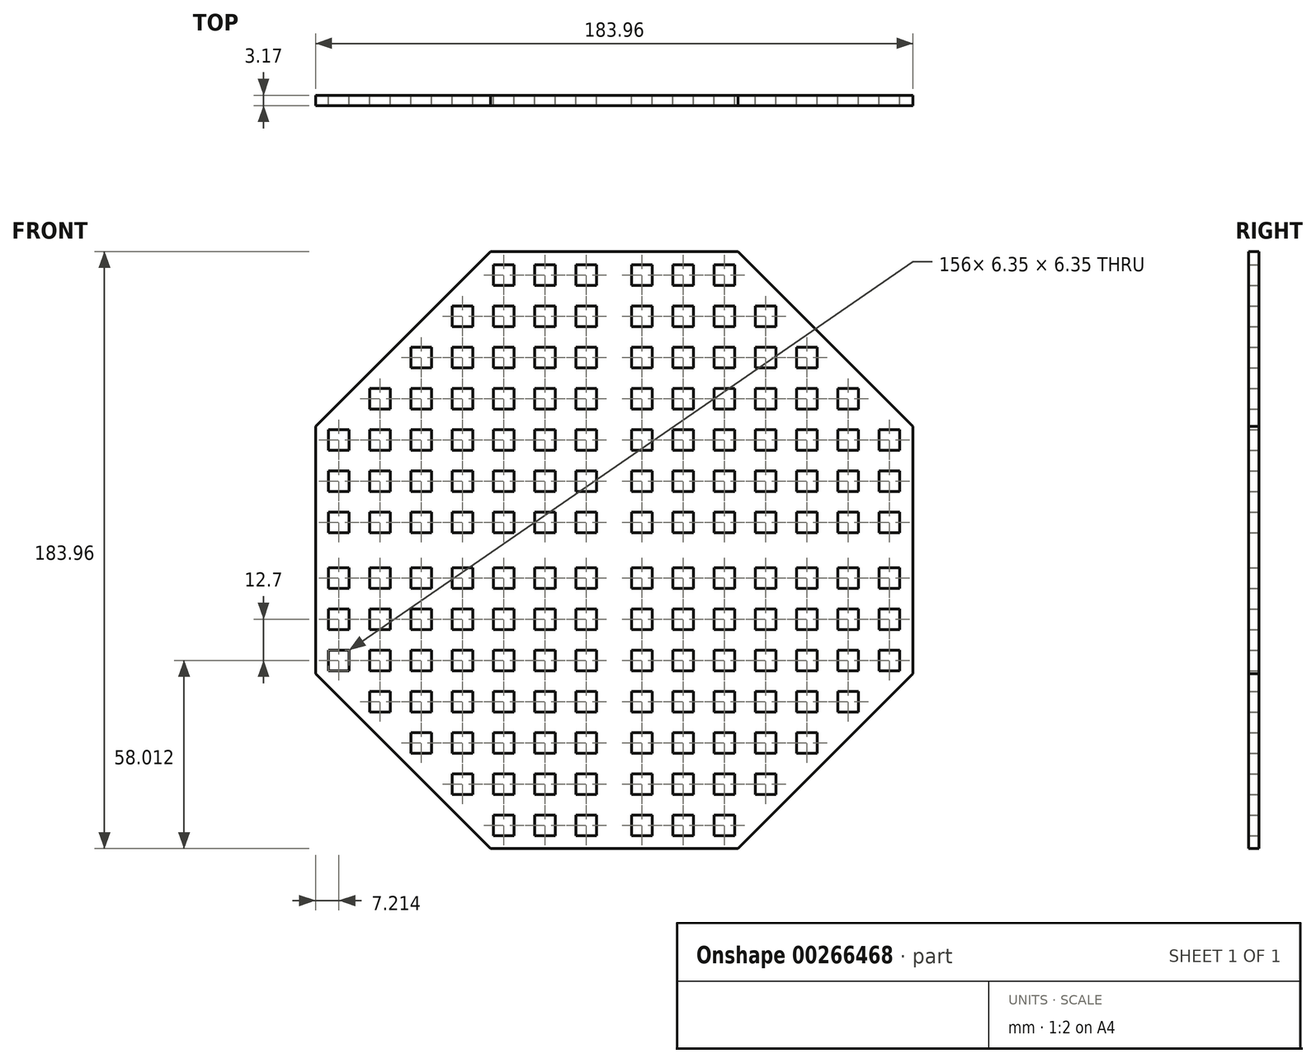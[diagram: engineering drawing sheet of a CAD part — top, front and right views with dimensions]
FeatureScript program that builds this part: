
annotation { "Feature Type Name" : "Feature", "Feature Type Description" : "" }
export const myFeature = defineFeature(function(context is Context, id is Id, definition is map)
    precondition{}
    {
        {
            var Q0;
            Q0=qCreatedBy(makeId("Front.planeOp"),FACE);
            var sketch = newSketch(context, id + "F0", { "sketchPlane" : qUnion([Q0])});
            skCircle(sketch, "E0.cCircle", {"center": v(3.14, 0) * mm, "radius": 91.98 * mm, "construction": true});
            skLineSegment(sketch, "E0.0", {"start": v(95.12, 38.1) * mm, "end": v(95.12, -38.1) * mm});
            skLineSegment(sketch, "E0.1", {"start": v(95.12, -38.1) * mm, "end": v(41.24, -91.98) * mm});
            skLineSegment(sketch, "E0.2", {"start": v(41.24, -91.98) * mm, "end": v(-34.96, -91.98) * mm});
            skLineSegment(sketch, "E0.3", {"start": v(-34.96, -91.98) * mm, "end": v(-88.84, -38.1) * mm});
            skLineSegment(sketch, "E0.4", {"start": v(-88.84, -38.1) * mm, "end": v(-88.84, 38.1) * mm});
            skLineSegment(sketch, "E0.5", {"start": v(-88.84, 38.1) * mm, "end": v(-34.96, 91.98) * mm});
            skLineSegment(sketch, "E0.6", {"start": v(-34.96, 91.98) * mm, "end": v(41.24, 91.98) * mm});
            skLineSegment(sketch, "E0.7", {"start": v(41.24, 91.98) * mm, "end": v(95.12, 38.1) * mm});
            skPoint(sketch, "E0.0.midPoint", {"position": v(95.12, 0) * mm});
            skLineSegment(sketch, "E1.0.4.0", {"start": v(-84.8, 37.14) * mm, "end": v(-78.45, 37.14) * mm});
            skLineSegment(sketch, "E1.0.4.1", {"start": v(-84.8, 37.14) * mm, "end": v(-84.8, 30.8) * mm});
            skLineSegment(sketch, "E1.0.4.2", {"start": v(-84.8, 30.8) * mm, "end": v(-78.45, 30.8) * mm});
            skLineSegment(sketch, "E1.0.4.3", {"start": v(-78.45, 37.14) * mm, "end": v(-78.45, 30.8) * mm});
            skLineSegment(sketch, "E1.0.5.0", {"start": v(-84.8, 24.44) * mm, "end": v(-78.45, 24.44) * mm});
            skLineSegment(sketch, "E1.0.5.1", {"start": v(-84.8, 24.44) * mm, "end": v(-84.8, 18.1) * mm});
            skLineSegment(sketch, "E1.0.5.2", {"start": v(-84.8, 18.1) * mm, "end": v(-78.45, 18.1) * mm});
            skLineSegment(sketch, "E1.0.5.3", {"start": v(-78.45, 24.44) * mm, "end": v(-78.45, 18.1) * mm});
            skLineSegment(sketch, "E1.0.6.0", {"start": v(-84.8, 11.74) * mm, "end": v(-78.45, 11.74) * mm});
            skLineSegment(sketch, "E1.0.6.1", {"start": v(-84.8, 11.74) * mm, "end": v(-84.8, 5.4) * mm});
            skLineSegment(sketch, "E1.0.6.2", {"start": v(-84.8, 5.4) * mm, "end": v(-78.45, 5.4) * mm});
            skLineSegment(sketch, "E1.0.6.3", {"start": v(-78.45, 11.74) * mm, "end": v(-78.45, 5.4) * mm});
            skLineSegment(sketch, "E1.1.3.0", {"start": v(-72.1, 49.84) * mm, "end": v(-65.75, 49.84) * mm});
            skLineSegment(sketch, "E1.1.3.1", {"start": v(-72.1, 49.84) * mm, "end": v(-72.1, 43.5) * mm});
            skLineSegment(sketch, "E1.1.3.2", {"start": v(-72.1, 43.5) * mm, "end": v(-65.75, 43.5) * mm});
            skLineSegment(sketch, "E1.1.3.3", {"start": v(-65.75, 49.84) * mm, "end": v(-65.75, 43.5) * mm});
            skLineSegment(sketch, "E1.1.4.0", {"start": v(-72.1, 37.14) * mm, "end": v(-65.75, 37.14) * mm});
            skLineSegment(sketch, "E1.1.4.1", {"start": v(-72.1, 37.14) * mm, "end": v(-72.1, 30.8) * mm});
            skLineSegment(sketch, "E1.1.4.2", {"start": v(-72.1, 30.8) * mm, "end": v(-65.75, 30.8) * mm});
            skLineSegment(sketch, "E1.1.4.3", {"start": v(-65.75, 37.14) * mm, "end": v(-65.75, 30.8) * mm});
            skLineSegment(sketch, "E1.1.5.0", {"start": v(-72.1, 24.44) * mm, "end": v(-65.75, 24.44) * mm});
            skLineSegment(sketch, "E1.1.5.1", {"start": v(-72.1, 24.44) * mm, "end": v(-72.1, 18.1) * mm});
            skLineSegment(sketch, "E1.1.5.2", {"start": v(-72.1, 18.1) * mm, "end": v(-65.75, 18.1) * mm});
            skLineSegment(sketch, "E1.1.5.3", {"start": v(-65.75, 24.44) * mm, "end": v(-65.75, 18.1) * mm});
            skLineSegment(sketch, "E1.1.6.0", {"start": v(-72.1, 11.74) * mm, "end": v(-65.75, 11.74) * mm});
            skLineSegment(sketch, "E1.1.6.1", {"start": v(-72.1, 11.74) * mm, "end": v(-72.1, 5.4) * mm});
            skLineSegment(sketch, "E1.1.6.2", {"start": v(-72.1, 5.4) * mm, "end": v(-65.75, 5.4) * mm});
            skLineSegment(sketch, "E1.1.6.3", {"start": v(-65.75, 11.74) * mm, "end": v(-65.75, 5.4) * mm});
            skLineSegment(sketch, "E1.2.2.0", {"start": v(-59.4, 62.54) * mm, "end": v(-53.05, 62.54) * mm});
            skLineSegment(sketch, "E1.2.2.1", {"start": v(-59.4, 62.54) * mm, "end": v(-59.4, 56.2) * mm});
            skLineSegment(sketch, "E1.2.2.2", {"start": v(-59.4, 56.2) * mm, "end": v(-53.05, 56.2) * mm});
            skLineSegment(sketch, "E1.2.2.3", {"start": v(-53.05, 62.54) * mm, "end": v(-53.05, 56.2) * mm});
            skLineSegment(sketch, "E1.2.3.0", {"start": v(-59.4, 49.84) * mm, "end": v(-53.05, 49.84) * mm});
            skLineSegment(sketch, "E1.2.3.1", {"start": v(-59.4, 49.84) * mm, "end": v(-59.4, 43.5) * mm});
            skLineSegment(sketch, "E1.2.3.2", {"start": v(-59.4, 43.5) * mm, "end": v(-53.05, 43.5) * mm});
            skLineSegment(sketch, "E1.2.3.3", {"start": v(-53.05, 49.84) * mm, "end": v(-53.05, 43.5) * mm});
            skLineSegment(sketch, "E1.2.4.0", {"start": v(-59.4, 37.14) * mm, "end": v(-53.05, 37.14) * mm});
            skLineSegment(sketch, "E1.2.4.1", {"start": v(-59.4, 37.14) * mm, "end": v(-59.4, 30.8) * mm});
            skLineSegment(sketch, "E1.2.4.2", {"start": v(-59.4, 30.8) * mm, "end": v(-53.05, 30.8) * mm});
            skLineSegment(sketch, "E1.2.4.3", {"start": v(-53.05, 37.14) * mm, "end": v(-53.05, 30.8) * mm});
            skLineSegment(sketch, "E1.2.5.0", {"start": v(-59.4, 24.44) * mm, "end": v(-53.05, 24.44) * mm});
            skLineSegment(sketch, "E1.2.5.1", {"start": v(-59.4, 24.44) * mm, "end": v(-59.4, 18.1) * mm});
            skLineSegment(sketch, "E1.2.5.2", {"start": v(-59.4, 18.1) * mm, "end": v(-53.05, 18.1) * mm});
            skLineSegment(sketch, "E1.2.5.3", {"start": v(-53.05, 24.44) * mm, "end": v(-53.05, 18.1) * mm});
            skLineSegment(sketch, "E1.2.6.0", {"start": v(-59.4, 11.74) * mm, "end": v(-53.05, 11.74) * mm});
            skLineSegment(sketch, "E1.2.6.1", {"start": v(-59.4, 11.74) * mm, "end": v(-59.4, 5.4) * mm});
            skLineSegment(sketch, "E1.2.6.2", {"start": v(-59.4, 5.4) * mm, "end": v(-53.05, 5.4) * mm});
            skLineSegment(sketch, "E1.2.6.3", {"start": v(-53.05, 11.74) * mm, "end": v(-53.05, 5.4) * mm});
            skLineSegment(sketch, "E1.3.1.0", {"start": v(-46.7, 75.24) * mm, "end": v(-40.35, 75.24) * mm});
            skLineSegment(sketch, "E1.3.1.1", {"start": v(-46.7, 75.24) * mm, "end": v(-46.7, 68.9) * mm});
            skLineSegment(sketch, "E1.3.1.2", {"start": v(-46.7, 68.9) * mm, "end": v(-40.35, 68.9) * mm});
            skLineSegment(sketch, "E1.3.1.3", {"start": v(-40.35, 75.24) * mm, "end": v(-40.35, 68.9) * mm});
            skLineSegment(sketch, "E1.3.2.0", {"start": v(-46.7, 62.54) * mm, "end": v(-40.35, 62.54) * mm});
            skLineSegment(sketch, "E1.3.2.1", {"start": v(-46.7, 62.54) * mm, "end": v(-46.7, 56.2) * mm});
            skLineSegment(sketch, "E1.3.2.2", {"start": v(-46.7, 56.2) * mm, "end": v(-40.35, 56.2) * mm});
            skLineSegment(sketch, "E1.3.2.3", {"start": v(-40.35, 62.54) * mm, "end": v(-40.35, 56.2) * mm});
            skLineSegment(sketch, "E1.3.3.0", {"start": v(-46.7, 49.84) * mm, "end": v(-40.35, 49.84) * mm});
            skLineSegment(sketch, "E1.3.3.1", {"start": v(-46.7, 49.84) * mm, "end": v(-46.7, 43.5) * mm});
            skLineSegment(sketch, "E1.3.3.2", {"start": v(-46.7, 43.5) * mm, "end": v(-40.35, 43.5) * mm});
            skLineSegment(sketch, "E1.3.3.3", {"start": v(-40.35, 49.84) * mm, "end": v(-40.35, 43.5) * mm});
            skLineSegment(sketch, "E1.3.4.0", {"start": v(-46.7, 37.14) * mm, "end": v(-40.35, 37.14) * mm});
            skLineSegment(sketch, "E1.3.4.1", {"start": v(-46.7, 37.14) * mm, "end": v(-46.7, 30.8) * mm});
            skLineSegment(sketch, "E1.3.4.2", {"start": v(-46.7, 30.8) * mm, "end": v(-40.35, 30.8) * mm});
            skLineSegment(sketch, "E1.3.4.3", {"start": v(-40.35, 37.14) * mm, "end": v(-40.35, 30.8) * mm});
            skLineSegment(sketch, "E1.3.5.0", {"start": v(-46.7, 24.44) * mm, "end": v(-40.35, 24.44) * mm});
            skLineSegment(sketch, "E1.3.5.1", {"start": v(-46.7, 24.44) * mm, "end": v(-46.7, 18.1) * mm});
            skLineSegment(sketch, "E1.3.5.2", {"start": v(-46.7, 18.1) * mm, "end": v(-40.35, 18.1) * mm});
            skLineSegment(sketch, "E1.3.5.3", {"start": v(-40.35, 24.44) * mm, "end": v(-40.35, 18.1) * mm});
            skLineSegment(sketch, "E1.3.6.0", {"start": v(-46.7, 11.74) * mm, "end": v(-40.35, 11.74) * mm});
            skLineSegment(sketch, "E1.3.6.1", {"start": v(-46.7, 11.74) * mm, "end": v(-46.7, 5.4) * mm});
            skLineSegment(sketch, "E1.3.6.2", {"start": v(-46.7, 5.4) * mm, "end": v(-40.35, 5.4) * mm});
            skLineSegment(sketch, "E1.3.6.3", {"start": v(-40.35, 11.74) * mm, "end": v(-40.35, 5.4) * mm});
            skLineSegment(sketch, "E1.4.0.0", {"start": v(-34, 87.94) * mm, "end": v(-27.65, 87.94) * mm});
            skLineSegment(sketch, "E1.4.0.1", {"start": v(-34, 87.94) * mm, "end": v(-34, 81.6) * mm});
            skLineSegment(sketch, "E1.4.0.2", {"start": v(-34, 81.6) * mm, "end": v(-27.65, 81.6) * mm});
            skLineSegment(sketch, "E1.4.0.3", {"start": v(-27.65, 87.94) * mm, "end": v(-27.65, 81.6) * mm});
            skLineSegment(sketch, "E1.4.1.0", {"start": v(-34, 75.24) * mm, "end": v(-27.65, 75.24) * mm});
            skLineSegment(sketch, "E1.4.1.1", {"start": v(-34, 75.24) * mm, "end": v(-34, 68.9) * mm});
            skLineSegment(sketch, "E1.4.1.2", {"start": v(-34, 68.9) * mm, "end": v(-27.65, 68.9) * mm});
            skLineSegment(sketch, "E1.4.1.3", {"start": v(-27.65, 75.24) * mm, "end": v(-27.65, 68.9) * mm});
            skLineSegment(sketch, "E1.4.2.0", {"start": v(-34, 62.54) * mm, "end": v(-27.65, 62.54) * mm});
            skLineSegment(sketch, "E1.4.2.1", {"start": v(-34, 62.54) * mm, "end": v(-34, 56.2) * mm});
            skLineSegment(sketch, "E1.4.2.2", {"start": v(-34, 56.2) * mm, "end": v(-27.65, 56.2) * mm});
            skLineSegment(sketch, "E1.4.2.3", {"start": v(-27.65, 62.54) * mm, "end": v(-27.65, 56.2) * mm});
            skLineSegment(sketch, "E1.4.3.0", {"start": v(-34, 49.84) * mm, "end": v(-27.65, 49.84) * mm});
            skLineSegment(sketch, "E1.4.3.1", {"start": v(-34, 49.84) * mm, "end": v(-34, 43.5) * mm});
            skLineSegment(sketch, "E1.4.3.2", {"start": v(-34, 43.5) * mm, "end": v(-27.65, 43.5) * mm});
            skLineSegment(sketch, "E1.4.3.3", {"start": v(-27.65, 49.84) * mm, "end": v(-27.65, 43.5) * mm});
            skLineSegment(sketch, "E1.4.4.0", {"start": v(-34, 37.14) * mm, "end": v(-27.65, 37.14) * mm});
            skLineSegment(sketch, "E1.4.4.1", {"start": v(-34, 37.14) * mm, "end": v(-34, 30.8) * mm});
            skLineSegment(sketch, "E1.4.4.2", {"start": v(-34, 30.8) * mm, "end": v(-27.65, 30.8) * mm});
            skLineSegment(sketch, "E1.4.4.3", {"start": v(-27.65, 37.14) * mm, "end": v(-27.65, 30.8) * mm});
            skLineSegment(sketch, "E1.4.5.0", {"start": v(-34, 24.44) * mm, "end": v(-27.65, 24.44) * mm});
            skLineSegment(sketch, "E1.4.5.1", {"start": v(-34, 24.44) * mm, "end": v(-34, 18.1) * mm});
            skLineSegment(sketch, "E1.4.5.2", {"start": v(-34, 18.1) * mm, "end": v(-27.65, 18.1) * mm});
            skLineSegment(sketch, "E1.4.5.3", {"start": v(-27.65, 24.44) * mm, "end": v(-27.65, 18.1) * mm});
            skLineSegment(sketch, "E1.4.6.0", {"start": v(-34, 11.74) * mm, "end": v(-27.65, 11.74) * mm});
            skLineSegment(sketch, "E1.4.6.1", {"start": v(-34, 11.74) * mm, "end": v(-34, 5.4) * mm});
            skLineSegment(sketch, "E1.4.6.2", {"start": v(-34, 5.4) * mm, "end": v(-27.65, 5.4) * mm});
            skLineSegment(sketch, "E1.4.6.3", {"start": v(-27.65, 11.74) * mm, "end": v(-27.65, 5.4) * mm});
            skLineSegment(sketch, "E1.5.0.0", {"start": v(-21.3, 87.94) * mm, "end": v(-14.95, 87.94) * mm});
            skLineSegment(sketch, "E1.5.0.1", {"start": v(-21.3, 87.94) * mm, "end": v(-21.3, 81.6) * mm});
            skLineSegment(sketch, "E1.5.0.2", {"start": v(-21.3, 81.6) * mm, "end": v(-14.95, 81.6) * mm});
            skLineSegment(sketch, "E1.5.0.3", {"start": v(-14.95, 87.94) * mm, "end": v(-14.95, 81.6) * mm});
            skLineSegment(sketch, "E1.5.1.0", {"start": v(-21.3, 75.24) * mm, "end": v(-14.95, 75.24) * mm});
            skLineSegment(sketch, "E1.5.1.1", {"start": v(-21.3, 75.24) * mm, "end": v(-21.3, 68.9) * mm});
            skLineSegment(sketch, "E1.5.1.2", {"start": v(-21.3, 68.9) * mm, "end": v(-14.95, 68.9) * mm});
            skLineSegment(sketch, "E1.5.1.3", {"start": v(-14.95, 75.24) * mm, "end": v(-14.95, 68.9) * mm});
            skLineSegment(sketch, "E1.5.2.0", {"start": v(-21.3, 62.54) * mm, "end": v(-14.95, 62.54) * mm});
            skLineSegment(sketch, "E1.5.2.1", {"start": v(-21.3, 62.54) * mm, "end": v(-21.3, 56.2) * mm});
            skLineSegment(sketch, "E1.5.2.2", {"start": v(-21.3, 56.2) * mm, "end": v(-14.95, 56.2) * mm});
            skLineSegment(sketch, "E1.5.2.3", {"start": v(-14.95, 62.54) * mm, "end": v(-14.95, 56.2) * mm});
            skLineSegment(sketch, "E1.5.3.0", {"start": v(-21.3, 49.84) * mm, "end": v(-14.95, 49.84) * mm});
            skLineSegment(sketch, "E1.5.3.1", {"start": v(-21.3, 49.84) * mm, "end": v(-21.3, 43.5) * mm});
            skLineSegment(sketch, "E1.5.3.2", {"start": v(-21.3, 43.5) * mm, "end": v(-14.95, 43.5) * mm});
            skLineSegment(sketch, "E1.5.3.3", {"start": v(-14.95, 49.84) * mm, "end": v(-14.95, 43.5) * mm});
            skLineSegment(sketch, "E1.5.4.0", {"start": v(-21.3, 37.14) * mm, "end": v(-14.95, 37.14) * mm});
            skLineSegment(sketch, "E1.5.4.1", {"start": v(-21.3, 37.14) * mm, "end": v(-21.3, 30.8) * mm});
            skLineSegment(sketch, "E1.5.4.2", {"start": v(-21.3, 30.8) * mm, "end": v(-14.95, 30.8) * mm});
            skLineSegment(sketch, "E1.5.4.3", {"start": v(-14.95, 37.14) * mm, "end": v(-14.95, 30.8) * mm});
            skLineSegment(sketch, "E1.5.5.0", {"start": v(-21.3, 24.44) * mm, "end": v(-14.95, 24.44) * mm});
            skLineSegment(sketch, "E1.5.5.1", {"start": v(-21.3, 24.44) * mm, "end": v(-21.3, 18.1) * mm});
            skLineSegment(sketch, "E1.5.5.2", {"start": v(-21.3, 18.1) * mm, "end": v(-14.95, 18.1) * mm});
            skLineSegment(sketch, "E1.5.5.3", {"start": v(-14.95, 24.44) * mm, "end": v(-14.95, 18.1) * mm});
            skLineSegment(sketch, "E1.5.6.0", {"start": v(-21.3, 11.74) * mm, "end": v(-14.95, 11.74) * mm});
            skLineSegment(sketch, "E1.5.6.1", {"start": v(-21.3, 11.74) * mm, "end": v(-21.3, 5.4) * mm});
            skLineSegment(sketch, "E1.5.6.2", {"start": v(-21.3, 5.4) * mm, "end": v(-14.95, 5.4) * mm});
            skLineSegment(sketch, "E1.5.6.3", {"start": v(-14.95, 11.74) * mm, "end": v(-14.95, 5.4) * mm});
            skLineSegment(sketch, "E1.6.0.0", {"start": v(-8.6, 87.94) * mm, "end": v(-2.25, 87.94) * mm});
            skLineSegment(sketch, "E1.6.0.1", {"start": v(-8.6, 87.94) * mm, "end": v(-8.6, 81.6) * mm});
            skLineSegment(sketch, "E1.6.0.2", {"start": v(-8.6, 81.6) * mm, "end": v(-2.25, 81.6) * mm});
            skLineSegment(sketch, "E1.6.0.3", {"start": v(-2.25, 87.94) * mm, "end": v(-2.25, 81.6) * mm});
            skLineSegment(sketch, "E1.6.1.0", {"start": v(-8.6, 75.24) * mm, "end": v(-2.25, 75.24) * mm});
            skLineSegment(sketch, "E1.6.1.1", {"start": v(-8.6, 75.24) * mm, "end": v(-8.6, 68.9) * mm});
            skLineSegment(sketch, "E1.6.1.2", {"start": v(-8.6, 68.9) * mm, "end": v(-2.25, 68.9) * mm});
            skLineSegment(sketch, "E1.6.1.3", {"start": v(-2.25, 75.24) * mm, "end": v(-2.25, 68.9) * mm});
            skLineSegment(sketch, "E1.6.2.0", {"start": v(-8.6, 62.54) * mm, "end": v(-2.25, 62.54) * mm});
            skLineSegment(sketch, "E1.6.2.1", {"start": v(-8.6, 62.54) * mm, "end": v(-8.6, 56.2) * mm});
            skLineSegment(sketch, "E1.6.2.2", {"start": v(-8.6, 56.2) * mm, "end": v(-2.25, 56.2) * mm});
            skLineSegment(sketch, "E1.6.2.3", {"start": v(-2.25, 62.54) * mm, "end": v(-2.25, 56.2) * mm});
            skLineSegment(sketch, "E1.6.3.0", {"start": v(-8.6, 49.84) * mm, "end": v(-2.25, 49.84) * mm});
            skLineSegment(sketch, "E1.6.3.1", {"start": v(-8.6, 49.84) * mm, "end": v(-8.6, 43.5) * mm});
            skLineSegment(sketch, "E1.6.3.2", {"start": v(-8.6, 43.5) * mm, "end": v(-2.25, 43.5) * mm});
            skLineSegment(sketch, "E1.6.3.3", {"start": v(-2.25, 49.84) * mm, "end": v(-2.25, 43.5) * mm});
            skLineSegment(sketch, "E1.6.4.0", {"start": v(-8.6, 37.14) * mm, "end": v(-2.25, 37.14) * mm});
            skLineSegment(sketch, "E1.6.4.1", {"start": v(-8.6, 37.14) * mm, "end": v(-8.6, 30.8) * mm});
            skLineSegment(sketch, "E1.6.4.2", {"start": v(-8.6, 30.8) * mm, "end": v(-2.25, 30.8) * mm});
            skLineSegment(sketch, "E1.6.4.3", {"start": v(-2.25, 37.14) * mm, "end": v(-2.25, 30.8) * mm});
            skLineSegment(sketch, "E1.6.5.0", {"start": v(-8.6, 24.44) * mm, "end": v(-2.25, 24.44) * mm});
            skLineSegment(sketch, "E1.6.5.1", {"start": v(-8.6, 24.44) * mm, "end": v(-8.6, 18.1) * mm});
            skLineSegment(sketch, "E1.6.5.2", {"start": v(-8.6, 18.1) * mm, "end": v(-2.25, 18.1) * mm});
            skLineSegment(sketch, "E1.6.5.3", {"start": v(-2.25, 24.44) * mm, "end": v(-2.25, 18.1) * mm});
            skLineSegment(sketch, "E1.6.6.0", {"start": v(-8.6, 11.74) * mm, "end": v(-2.25, 11.74) * mm});
            skLineSegment(sketch, "E1.6.6.1", {"start": v(-8.6, 11.74) * mm, "end": v(-8.6, 5.4) * mm});
            skLineSegment(sketch, "E1.6.6.2", {"start": v(-8.6, 5.4) * mm, "end": v(-2.25, 5.4) * mm});
            skLineSegment(sketch, "E1.6.6.3", {"start": v(-2.25, 11.74) * mm, "end": v(-2.25, 5.4) * mm});
            skLineSegment(sketch, "E2.MirrorCS", {"start": v(52.99, 68.9) * mm, "end": v(46.64, 68.9) * mm});
            skLineSegment(sketch, "E3.MirrorCS", {"start": v(59.34, 62.54) * mm, "end": v(59.34, 56.2) * mm});
            skLineSegment(sketch, "E4.MirrorCS", {"start": v(33.94, 75.24) * mm, "end": v(33.94, 68.9) * mm});
            skLineSegment(sketch, "E5.MirrorCS", {"start": v(21.24, 62.54) * mm, "end": v(21.24, 56.2) * mm});
            skLineSegment(sketch, "E6.MirrorCS", {"start": v(33.94, 24.44) * mm, "end": v(33.94, 18.1) * mm});
            skLineSegment(sketch, "E7.MirrorCS", {"start": v(72.04, 49.84) * mm, "end": v(72.04, 43.5) * mm});
            skLineSegment(sketch, "E8.MirrorCS", {"start": v(21.24, 11.74) * mm, "end": v(21.24, 5.4) * mm});
            skLineSegment(sketch, "E9.MirrorCS", {"start": v(8.54, 49.84) * mm, "end": v(8.54, 43.5) * mm});
            skLineSegment(sketch, "E10.MirrorCS", {"start": v(84.74, 24.44) * mm, "end": v(84.74, 18.1) * mm});
            skLineSegment(sketch, "E11.MirrorCS", {"start": v(46.64, 11.74) * mm, "end": v(46.64, 5.4) * mm});
            skLineSegment(sketch, "E12.MirrorCS", {"start": v(46.64, 62.54) * mm, "end": v(46.64, 56.2) * mm});
            skLineSegment(sketch, "E13.MirrorCS", {"start": v(72.04, 24.44) * mm, "end": v(72.04, 18.1) * mm});
            skLineSegment(sketch, "E14.MirrorCS", {"start": v(52.99, 62.54) * mm, "end": v(46.64, 62.54) * mm});
            skLineSegment(sketch, "E15.MirrorCS", {"start": v(40.29, 5.4) * mm, "end": v(33.94, 5.4) * mm});
            skLineSegment(sketch, "E16.MirrorCS", {"start": v(40.29, 56.2) * mm, "end": v(33.94, 56.2) * mm});
            skLineSegment(sketch, "E17.MirrorCS", {"start": v(27.59, 24.44) * mm, "end": v(27.59, 18.1) * mm});
            skLineSegment(sketch, "E18.MirrorCS", {"start": v(52.99, 18.1) * mm, "end": v(46.64, 18.1) * mm});
            skLineSegment(sketch, "E19.MirrorCS", {"start": v(52.99, 11.74) * mm, "end": v(46.64, 11.74) * mm});
            skLineSegment(sketch, "E20.MirrorCS", {"start": v(52.99, 24.44) * mm, "end": v(46.64, 24.44) * mm});
            skLineSegment(sketch, "E21.MirrorCS", {"start": v(46.64, 75.24) * mm, "end": v(46.64, 68.9) * mm});
            skLineSegment(sketch, "E22.MirrorCS", {"start": v(14.89, 75.24) * mm, "end": v(14.89, 68.9) * mm});
            skLineSegment(sketch, "E23.MirrorCS", {"start": v(59.34, 49.84) * mm, "end": v(59.34, 43.5) * mm});
            skLineSegment(sketch, "E24.MirrorCS", {"start": v(52.99, 37.14) * mm, "end": v(46.64, 37.14) * mm});
            skLineSegment(sketch, "E25.MirrorCS", {"start": v(84.74, 11.74) * mm, "end": v(84.74, 5.4) * mm});
            skLineSegment(sketch, "E26.MirrorCS", {"start": v(46.64, 49.84) * mm, "end": v(46.64, 43.5) * mm});
            skLineSegment(sketch, "E27.MirrorCS", {"start": v(40.29, 30.8) * mm, "end": v(33.94, 30.8) * mm});
            skLineSegment(sketch, "E28.MirrorCS", {"start": v(33.94, 62.54) * mm, "end": v(33.94, 56.2) * mm});
            skLineSegment(sketch, "E29.MirrorCS", {"start": v(40.29, 49.84) * mm, "end": v(33.94, 49.84) * mm});
            skLineSegment(sketch, "E30.MirrorCS", {"start": v(27.59, 49.84) * mm, "end": v(27.59, 43.5) * mm});
            skLineSegment(sketch, "E31.MirrorCS", {"start": v(59.34, 24.44) * mm, "end": v(59.34, 18.1) * mm});
            skLineSegment(sketch, "E32.MirrorCS", {"start": v(72.04, 11.74) * mm, "end": v(72.04, 5.4) * mm});
            skLineSegment(sketch, "E33.MirrorCS", {"start": v(14.89, 62.54) * mm, "end": v(14.89, 56.2) * mm});
            skLineSegment(sketch, "E34.MirrorCS", {"start": v(52.99, 43.5) * mm, "end": v(46.64, 43.5) * mm});
            skLineSegment(sketch, "E35.MirrorCS", {"start": v(40.29, 81.6) * mm, "end": v(33.94, 81.6) * mm});
            skLineSegment(sketch, "E36.MirrorCS", {"start": v(33.94, 11.74) * mm, "end": v(33.94, 5.4) * mm});
            skLineSegment(sketch, "E37.MirrorCS", {"start": v(91.09, 5.4) * mm, "end": v(84.74, 5.4) * mm});
            skLineSegment(sketch, "E38.MirrorCS", {"start": v(21.24, 49.84) * mm, "end": v(21.24, 43.5) * mm});
            skLineSegment(sketch, "E39.MirrorCS", {"start": v(52.99, 75.24) * mm, "end": v(46.64, 75.24) * mm});
            skLineSegment(sketch, "E40.MirrorCS", {"start": v(21.24, 24.44) * mm, "end": v(21.24, 18.1) * mm});
            skLineSegment(sketch, "E41.MirrorCS", {"start": v(8.54, 62.54) * mm, "end": v(8.54, 56.2) * mm});
            skLineSegment(sketch, "E42.MirrorCS", {"start": v(21.24, 75.24) * mm, "end": v(21.24, 68.9) * mm});
            skLineSegment(sketch, "E43.MirrorCS", {"start": v(8.54, 11.74) * mm, "end": v(8.54, 5.4) * mm});
            skLineSegment(sketch, "E44.MirrorCS", {"start": v(52.99, 11.74) * mm, "end": v(52.99, 5.4) * mm});
            skLineSegment(sketch, "E45.MirrorCS", {"start": v(52.99, 24.44) * mm, "end": v(52.99, 18.1) * mm});
            skLineSegment(sketch, "E46.MirrorCS", {"start": v(52.99, 62.54) * mm, "end": v(52.99, 56.2) * mm});
            skLineSegment(sketch, "E47.MirrorCS", {"start": v(46.64, 24.44) * mm, "end": v(46.64, 18.1) * mm});
            skLineSegment(sketch, "E48.MirrorCS", {"start": v(27.59, 75.24) * mm, "end": v(27.59, 68.9) * mm});
            skLineSegment(sketch, "E49.MirrorCS", {"start": v(65.69, 24.44) * mm, "end": v(65.69, 18.1) * mm});
            skLineSegment(sketch, "E50.MirrorCS", {"start": v(14.89, 11.74) * mm, "end": v(14.89, 5.4) * mm});
            skLineSegment(sketch, "E51.MirrorCS", {"start": v(52.99, 49.84) * mm, "end": v(52.99, 43.5) * mm});
            skLineSegment(sketch, "E52.MirrorCS", {"start": v(91.09, 11.74) * mm, "end": v(91.09, 5.4) * mm});
            skLineSegment(sketch, "E53.MirrorCS", {"start": v(78.39, 11.74) * mm, "end": v(78.39, 5.4) * mm});
            skLineSegment(sketch, "E54.MirrorCS", {"start": v(40.29, 75.24) * mm, "end": v(40.29, 68.9) * mm});
            skLineSegment(sketch, "E55.MirrorCS", {"start": v(78.39, 49.84) * mm, "end": v(78.39, 43.5) * mm});
            skLineSegment(sketch, "E56.MirrorCS", {"start": v(65.69, 11.74) * mm, "end": v(65.69, 5.4) * mm});
            skLineSegment(sketch, "E57.MirrorCS", {"start": v(65.69, 62.54) * mm, "end": v(65.69, 56.2) * mm});
            skLineSegment(sketch, "E58.MirrorCS", {"start": v(14.89, 49.84) * mm, "end": v(14.89, 43.5) * mm});
            skLineSegment(sketch, "E59.MirrorCS", {"start": v(27.59, 11.74) * mm, "end": v(27.59, 5.4) * mm});
            skLineSegment(sketch, "E60.MirrorCS", {"start": v(27.59, 62.54) * mm, "end": v(27.59, 56.2) * mm});
            skLineSegment(sketch, "E61.MirrorCS", {"start": v(40.29, 24.44) * mm, "end": v(40.29, 18.1) * mm});
            skLineSegment(sketch, "E62.MirrorCS", {"start": v(40.29, 62.54) * mm, "end": v(40.29, 56.2) * mm});
            skLineSegment(sketch, "E63.MirrorCS", {"start": v(40.29, 24.44) * mm, "end": v(33.94, 24.44) * mm});
            skLineSegment(sketch, "E64.MirrorCS", {"start": v(78.39, 24.44) * mm, "end": v(78.39, 18.1) * mm});
            skLineSegment(sketch, "E65.MirrorCS", {"start": v(40.29, 49.84) * mm, "end": v(40.29, 43.5) * mm});
            skLineSegment(sketch, "E66.MirrorCS", {"start": v(40.29, 37.14) * mm, "end": v(33.94, 37.14) * mm});
            skLineSegment(sketch, "E67.MirrorCS", {"start": v(59.34, 11.74) * mm, "end": v(59.34, 5.4) * mm});
            skLineSegment(sketch, "E68.MirrorCS", {"start": v(52.99, 49.84) * mm, "end": v(46.64, 49.84) * mm});
            skLineSegment(sketch, "E69.MirrorCS", {"start": v(40.29, 18.1) * mm, "end": v(33.94, 18.1) * mm});
            skLineSegment(sketch, "E70.MirrorCS", {"start": v(40.29, 68.9) * mm, "end": v(33.94, 68.9) * mm});
            skLineSegment(sketch, "E71.MirrorCS", {"start": v(52.99, 30.8) * mm, "end": v(46.64, 30.8) * mm});
            skLineSegment(sketch, "E72.MirrorCS", {"start": v(8.54, 24.44) * mm, "end": v(8.54, 18.1) * mm});
            skLineSegment(sketch, "E73.MirrorCS", {"start": v(33.94, 49.84) * mm, "end": v(33.94, 43.5) * mm});
            skLineSegment(sketch, "E74.MirrorCS", {"start": v(40.29, 62.54) * mm, "end": v(33.94, 62.54) * mm});
            skLineSegment(sketch, "E75.MirrorCS", {"start": v(40.29, 11.74) * mm, "end": v(40.29, 5.4) * mm});
            skLineSegment(sketch, "E76.MirrorCS", {"start": v(40.29, 43.5) * mm, "end": v(33.94, 43.5) * mm});
            skLineSegment(sketch, "E77.MirrorCS", {"start": v(8.54, 75.24) * mm, "end": v(8.54, 68.9) * mm});
            skLineSegment(sketch, "E78.MirrorCS", {"start": v(91.09, 24.44) * mm, "end": v(84.74, 24.44) * mm});
            skLineSegment(sketch, "E79.MirrorCS", {"start": v(14.89, 24.44) * mm, "end": v(14.89, 18.1) * mm});
            skLineSegment(sketch, "E80.MirrorCS", {"start": v(91.09, 30.8) * mm, "end": v(84.74, 30.8) * mm});
            skLineSegment(sketch, "E81.MirrorCS", {"start": v(40.29, 11.74) * mm, "end": v(33.94, 11.74) * mm});
            skLineSegment(sketch, "E82.MirrorCS", {"start": v(40.29, 87.94) * mm, "end": v(33.94, 87.94) * mm});
            skLineSegment(sketch, "E83.MirrorCS", {"start": v(91.09, 11.74) * mm, "end": v(84.74, 11.74) * mm});
            skLineSegment(sketch, "E84.MirrorCS", {"start": v(91.09, 24.44) * mm, "end": v(91.09, 18.1) * mm});
            skLineSegment(sketch, "E85.MirrorCS", {"start": v(52.99, 5.4) * mm, "end": v(46.64, 5.4) * mm});
            skLineSegment(sketch, "E86.MirrorCS", {"start": v(52.99, 56.2) * mm, "end": v(46.64, 56.2) * mm});
            skLineSegment(sketch, "E87.MirrorCS", {"start": v(40.29, 75.24) * mm, "end": v(33.94, 75.24) * mm});
            skLineSegment(sketch, "E88.MirrorCS", {"start": v(91.09, 18.1) * mm, "end": v(84.74, 18.1) * mm});
            skLineSegment(sketch, "E89.MirrorCS", {"start": v(91.09, 37.14) * mm, "end": v(84.74, 37.14) * mm});
            skLineSegment(sketch, "E90.MirrorCS", {"start": v(65.69, 49.84) * mm, "end": v(65.69, 43.5) * mm});
            skLineSegment(sketch, "E91.MirrorCS", {"start": v(52.99, 75.24) * mm, "end": v(52.99, 68.9) * mm});
            skLineSegment(sketch, "E92.MirrorCS", {"start": v(84.74, 37.14) * mm, "end": v(84.74, 30.8) * mm});
            skLineSegment(sketch, "E93.MirrorCS", {"start": v(46.64, 37.14) * mm, "end": v(46.64, 30.8) * mm});
            skLineSegment(sketch, "E94.MirrorCS", {"start": v(59.34, 37.14) * mm, "end": v(59.34, 30.8) * mm});
            skLineSegment(sketch, "E95.MirrorCS", {"start": v(14.89, 30.8) * mm, "end": v(8.54, 30.8) * mm});
            skLineSegment(sketch, "E96.MirrorCS", {"start": v(14.89, 81.6) * mm, "end": v(8.54, 81.6) * mm});
            skLineSegment(sketch, "E97.MirrorCS", {"start": v(78.39, 30.8) * mm, "end": v(72.04, 30.8) * mm});
            skLineSegment(sketch, "E98.MirrorCS", {"start": v(27.59, 43.5) * mm, "end": v(21.24, 43.5) * mm});
            skLineSegment(sketch, "E99.MirrorCS", {"start": v(78.39, 24.44) * mm, "end": v(72.04, 24.44) * mm});
            skLineSegment(sketch, "E100.MirrorCS", {"start": v(14.89, 75.24) * mm, "end": v(8.54, 75.24) * mm});
            skLineSegment(sketch, "E101.MirrorCS", {"start": v(14.89, 87.94) * mm, "end": v(8.54, 87.94) * mm});
            skLineSegment(sketch, "E102.MirrorCS", {"start": v(14.89, 37.14) * mm, "end": v(8.54, 37.14) * mm});
            skLineSegment(sketch, "E103.MirrorCS", {"start": v(65.69, 43.5) * mm, "end": v(59.34, 43.5) * mm});
            skLineSegment(sketch, "E104.MirrorCS", {"start": v(72.04, 37.14) * mm, "end": v(72.04, 30.8) * mm});
            skLineSegment(sketch, "E105.MirrorCS", {"start": v(78.39, 49.84) * mm, "end": v(72.04, 49.84) * mm});
            skLineSegment(sketch, "E106.MirrorCS", {"start": v(33.94, 87.94) * mm, "end": v(33.94, 81.6) * mm});
            skLineSegment(sketch, "E107.MirrorCS", {"start": v(27.59, 87.94) * mm, "end": v(21.24, 87.94) * mm});
            skLineSegment(sketch, "E108.MirrorCS", {"start": v(65.69, 30.8) * mm, "end": v(59.34, 30.8) * mm});
            skLineSegment(sketch, "E109.MirrorCS", {"start": v(14.89, 5.4) * mm, "end": v(8.54, 5.4) * mm});
            skLineSegment(sketch, "E110.MirrorCS", {"start": v(27.59, 68.9) * mm, "end": v(21.24, 68.9) * mm});
            skLineSegment(sketch, "E111.MirrorCS", {"start": v(27.59, 18.1) * mm, "end": v(21.24, 18.1) * mm});
            skLineSegment(sketch, "E112.MirrorCS", {"start": v(8.54, 37.14) * mm, "end": v(8.54, 30.8) * mm});
            skLineSegment(sketch, "E113.MirrorCS", {"start": v(65.69, 37.14) * mm, "end": v(59.34, 37.14) * mm});
            skLineSegment(sketch, "E114.MirrorCS", {"start": v(65.69, 18.1) * mm, "end": v(59.34, 18.1) * mm});
            skLineSegment(sketch, "E115.MirrorCS", {"start": v(27.59, 37.14) * mm, "end": v(21.24, 37.14) * mm});
            skLineSegment(sketch, "E116.MirrorCS", {"start": v(33.94, 37.14) * mm, "end": v(33.94, 30.8) * mm});
            skLineSegment(sketch, "E117.MirrorCS", {"start": v(8.54, 87.94) * mm, "end": v(8.54, 81.6) * mm});
            skLineSegment(sketch, "E118.MirrorCS", {"start": v(40.29, 37.14) * mm, "end": v(40.29, 30.8) * mm});
            skLineSegment(sketch, "E119.MirrorCS", {"start": v(40.29, 87.94) * mm, "end": v(40.29, 81.6) * mm});
            skLineSegment(sketch, "E120.MirrorCS", {"start": v(14.89, 56.2) * mm, "end": v(8.54, 56.2) * mm});
            skLineSegment(sketch, "E121.MirrorCS", {"start": v(78.39, 5.4) * mm, "end": v(72.04, 5.4) * mm});
            skLineSegment(sketch, "E122.MirrorCS", {"start": v(65.69, 11.74) * mm, "end": v(59.34, 11.74) * mm});
            skLineSegment(sketch, "E123.MirrorCS", {"start": v(65.69, 62.54) * mm, "end": v(59.34, 62.54) * mm});
            skLineSegment(sketch, "E124.MirrorCS", {"start": v(14.89, 49.84) * mm, "end": v(8.54, 49.84) * mm});
            skLineSegment(sketch, "E125.MirrorCS", {"start": v(52.99, 37.14) * mm, "end": v(52.99, 30.8) * mm});
            skLineSegment(sketch, "E126.MirrorCS", {"start": v(27.59, 62.54) * mm, "end": v(21.24, 62.54) * mm});
            skLineSegment(sketch, "E127.MirrorCS", {"start": v(27.59, 11.74) * mm, "end": v(21.24, 11.74) * mm});
            skLineSegment(sketch, "E128.MirrorCS", {"start": v(14.89, 24.44) * mm, "end": v(8.54, 24.44) * mm});
            skLineSegment(sketch, "E129.MirrorCS", {"start": v(65.69, 37.14) * mm, "end": v(65.69, 30.8) * mm});
            skLineSegment(sketch, "E130.MirrorCS", {"start": v(27.59, 37.14) * mm, "end": v(27.59, 30.8) * mm});
            skLineSegment(sketch, "E131.MirrorCS", {"start": v(27.59, 87.94) * mm, "end": v(27.59, 81.6) * mm});
            skLineSegment(sketch, "E132.MirrorCS", {"start": v(65.69, 5.4) * mm, "end": v(59.34, 5.4) * mm});
            skLineSegment(sketch, "E133.MirrorCS", {"start": v(95.12, 38.1) * mm, "end": v(41.24, 91.98) * mm});
            skLineSegment(sketch, "E134.MirrorCS", {"start": v(27.59, 75.24) * mm, "end": v(21.24, 75.24) * mm});
            skLineSegment(sketch, "E135.MirrorCS", {"start": v(27.59, 24.44) * mm, "end": v(21.24, 24.44) * mm});
            skLineSegment(sketch, "E136.MirrorCS", {"start": v(14.89, 62.54) * mm, "end": v(8.54, 62.54) * mm});
            skLineSegment(sketch, "E137.MirrorCS", {"start": v(78.39, 11.74) * mm, "end": v(72.04, 11.74) * mm});
            skLineSegment(sketch, "E138.MirrorCS", {"start": v(65.69, 24.44) * mm, "end": v(59.34, 24.44) * mm});
            skLineSegment(sketch, "E139.MirrorCS", {"start": v(65.69, 56.2) * mm, "end": v(59.34, 56.2) * mm});
            skLineSegment(sketch, "E140.MirrorCS", {"start": v(27.59, 56.2) * mm, "end": v(21.24, 56.2) * mm});
            skLineSegment(sketch, "E141.MirrorCS", {"start": v(78.39, 43.5) * mm, "end": v(72.04, 43.5) * mm});
            skLineSegment(sketch, "E142.MirrorCS", {"start": v(21.24, 87.94) * mm, "end": v(21.24, 81.6) * mm});
            skLineSegment(sketch, "E143.MirrorCS", {"start": v(21.24, 37.14) * mm, "end": v(21.24, 30.8) * mm});
            skLineSegment(sketch, "E144.MirrorCS", {"start": v(14.89, 37.14) * mm, "end": v(14.89, 30.8) * mm});
            skLineSegment(sketch, "E145.MirrorCS", {"start": v(78.39, 18.1) * mm, "end": v(72.04, 18.1) * mm});
            skLineSegment(sketch, "E146.MirrorCS", {"start": v(14.89, 68.9) * mm, "end": v(8.54, 68.9) * mm});
            skLineSegment(sketch, "E147.MirrorCS", {"start": v(27.59, 30.8) * mm, "end": v(21.24, 30.8) * mm});
            skLineSegment(sketch, "E148.MirrorCS", {"start": v(27.59, 81.6) * mm, "end": v(21.24, 81.6) * mm});
            skLineSegment(sketch, "E149.MirrorCS", {"start": v(14.89, 18.1) * mm, "end": v(8.54, 18.1) * mm});
            skLineSegment(sketch, "E150.MirrorCS", {"start": v(14.89, 87.94) * mm, "end": v(14.89, 81.6) * mm});
            skLineSegment(sketch, "E151.MirrorCS", {"start": v(27.59, 49.84) * mm, "end": v(21.24, 49.84) * mm});
            skLineSegment(sketch, "E152.MirrorCS", {"start": v(78.39, 37.14) * mm, "end": v(72.04, 37.14) * mm});
            skLineSegment(sketch, "E153.MirrorCS", {"start": v(14.89, 43.5) * mm, "end": v(8.54, 43.5) * mm});
            skLineSegment(sketch, "E154.MirrorCS", {"start": v(27.59, 5.4) * mm, "end": v(21.24, 5.4) * mm});
            skLineSegment(sketch, "E155.MirrorCS", {"start": v(65.69, 49.84) * mm, "end": v(59.34, 49.84) * mm});
            skLineSegment(sketch, "E156.MirrorCS", {"start": v(91.09, 37.14) * mm, "end": v(91.09, 30.8) * mm});
            skLineSegment(sketch, "E157.MirrorCS", {"start": v(78.39, 37.14) * mm, "end": v(78.39, 30.8) * mm});
            skLineSegment(sketch, "E158.MirrorCS", {"start": v(14.89, 11.74) * mm, "end": v(8.54, 11.74) * mm});
            skLineSegment(sketch, "E159.MirrorCS", {"start": v(-65.75, -37.14) * mm, "end": v(-65.75, -30.8) * mm});
            skLineSegment(sketch, "E160.MirrorCS", {"start": v(-84.8, -37.14) * mm, "end": v(-78.45, -37.14) * mm});
            skLineSegment(sketch, "E161.MirrorCS", {"start": v(-72.1, -30.8) * mm, "end": v(-65.75, -30.8) * mm});
            skLineSegment(sketch, "E162.MirrorCS", {"start": v(27.59, -43.5) * mm, "end": v(21.24, -43.5) * mm});
            skLineSegment(sketch, "E163.MirrorCS", {"start": v(40.29, -87.94) * mm, "end": v(33.94, -87.94) * mm});
            skLineSegment(sketch, "E164.MirrorCS", {"start": v(27.59, -11.74) * mm, "end": v(21.24, -11.74) * mm});
            skLineSegment(sketch, "E165.MirrorCS", {"start": v(21.24, -37.14) * mm, "end": v(21.24, -30.8) * mm});
            skLineSegment(sketch, "E166.MirrorCS", {"start": v(40.29, -37.14) * mm, "end": v(33.94, -37.14) * mm});
            skLineSegment(sketch, "E167.MirrorCS", {"start": v(27.59, -37.14) * mm, "end": v(27.59, -30.8) * mm});
            skLineSegment(sketch, "E168.MirrorCS", {"start": v(14.89, -68.9) * mm, "end": v(8.54, -68.9) * mm});
            skLineSegment(sketch, "E169.MirrorCS", {"start": v(-40.35, -24.44) * mm, "end": v(-40.35, -18.1) * mm});
            skLineSegment(sketch, "E170.MirrorCS", {"start": v(40.29, -75.24) * mm, "end": v(33.94, -75.24) * mm});
            skLineSegment(sketch, "E171.MirrorCS", {"start": v(-34, -87.94) * mm, "end": v(-27.65, -87.94) * mm});
            skLineSegment(sketch, "E172.MirrorCS", {"start": v(-8.6, -56.2) * mm, "end": v(-2.25, -56.2) * mm});
            skLineSegment(sketch, "E173.MirrorCS", {"start": v(-84.8, -11.74) * mm, "end": v(-78.45, -11.74) * mm});
            skLineSegment(sketch, "E174.MirrorCS", {"start": v(-21.3, -11.74) * mm, "end": v(-14.95, -11.74) * mm});
            skLineSegment(sketch, "E175.MirrorCS", {"start": v(-8.6, -11.74) * mm, "end": v(-2.25, -11.74) * mm});
            skLineSegment(sketch, "E176.MirrorCS", {"start": v(-2.25, -37.14) * mm, "end": v(-2.25, -30.8) * mm});
            skLineSegment(sketch, "E177.MirrorCS", {"start": v(14.89, -5.4) * mm, "end": v(8.54, -5.4) * mm});
            skLineSegment(sketch, "E178.MirrorCS", {"start": v(78.39, -49.84) * mm, "end": v(78.39, -43.5) * mm});
            skLineSegment(sketch, "E179.MirrorCS", {"start": v(-40.35, -49.84) * mm, "end": v(-40.35, -43.5) * mm});
            skLineSegment(sketch, "E180.MirrorCS", {"start": v(46.64, -37.14) * mm, "end": v(46.64, -30.8) * mm});
            skLineSegment(sketch, "E181.MirrorCS", {"start": v(40.29, -11.74) * mm, "end": v(33.94, -11.74) * mm});
            skLineSegment(sketch, "E182.MirrorCS", {"start": v(78.39, -5.4) * mm, "end": v(72.04, -5.4) * mm});
            skLineSegment(sketch, "E183.MirrorCS", {"start": v(-72.1, -49.84) * mm, "end": v(-65.75, -49.84) * mm});
            skLineSegment(sketch, "E184.MirrorCS", {"start": v(-34, -75.24) * mm, "end": v(-27.65, -75.24) * mm});
            skLineSegment(sketch, "E185.MirrorCS", {"start": v(78.39, -30.8) * mm, "end": v(72.04, -30.8) * mm});
            skLineSegment(sketch, "E186.MirrorCS", {"start": v(-27.65, -62.54) * mm, "end": v(-27.65, -56.2) * mm});
            skLineSegment(sketch, "E187.MirrorCS", {"start": v(-8.6, -49.84) * mm, "end": v(-2.25, -49.84) * mm});
            skLineSegment(sketch, "E188.MirrorCS", {"start": v(14.89, -62.54) * mm, "end": v(14.89, -56.2) * mm});
            skLineSegment(sketch, "E189.MirrorCS", {"start": v(-34, -49.84) * mm, "end": v(-34, -43.5) * mm});
            skLineSegment(sketch, "E190.MirrorCS", {"start": v(-21.3, -18.1) * mm, "end": v(-14.95, -18.1) * mm});
            skLineSegment(sketch, "E191.MirrorCS", {"start": v(-53.05, -49.84) * mm, "end": v(-53.05, -43.5) * mm});
            skLineSegment(sketch, "E192.MirrorCS", {"start": v(72.04, -49.84) * mm, "end": v(72.04, -43.5) * mm});
            skLineSegment(sketch, "E193.MirrorCS", {"start": v(59.34, -49.84) * mm, "end": v(59.34, -43.5) * mm});
            skLineSegment(sketch, "E194.MirrorCS", {"start": v(-34, -81.6) * mm, "end": v(-27.65, -81.6) * mm});
            skLineSegment(sketch, "E195.MirrorCS", {"start": v(27.59, -62.54) * mm, "end": v(21.24, -62.54) * mm});
            skLineSegment(sketch, "E196.MirrorCS", {"start": v(65.69, -62.54) * mm, "end": v(65.69, -56.2) * mm});
            skLineSegment(sketch, "E197.MirrorCS", {"start": v(14.89, -11.74) * mm, "end": v(8.54, -11.74) * mm});
            skLineSegment(sketch, "E198.MirrorCS", {"start": v(91.09, -37.14) * mm, "end": v(84.74, -37.14) * mm});
            skLineSegment(sketch, "E199.MirrorCS", {"start": v(-72.1, -11.74) * mm, "end": v(-65.75, -11.74) * mm});
            skLineSegment(sketch, "E200.MirrorCS", {"start": v(14.89, -43.5) * mm, "end": v(8.54, -43.5) * mm});
            skLineSegment(sketch, "E201.MirrorCS", {"start": v(27.59, -24.44) * mm, "end": v(21.24, -24.44) * mm});
            skLineSegment(sketch, "E202.MirrorCS", {"start": v(27.59, -68.9) * mm, "end": v(21.24, -68.9) * mm});
            skLineSegment(sketch, "E203.MirrorCS", {"start": v(40.29, -24.44) * mm, "end": v(33.94, -24.44) * mm});
            skLineSegment(sketch, "E204.MirrorCS", {"start": v(59.34, -37.14) * mm, "end": v(59.34, -30.8) * mm});
            skLineSegment(sketch, "E205.MirrorCS", {"start": v(-8.6, -62.54) * mm, "end": v(-2.25, -62.54) * mm});
            skLineSegment(sketch, "E206.MirrorCS", {"start": v(-65.75, -24.44) * mm, "end": v(-65.75, -18.1) * mm});
            skLineSegment(sketch, "E207.MirrorCS", {"start": v(27.59, -5.4) * mm, "end": v(21.24, -5.4) * mm});
            skLineSegment(sketch, "E208.MirrorCS", {"start": v(78.39, -49.84) * mm, "end": v(72.04, -49.84) * mm});
            skLineSegment(sketch, "E209.MirrorCS", {"start": v(-14.95, -49.84) * mm, "end": v(-14.95, -43.5) * mm});
            skLineSegment(sketch, "E210.MirrorCS", {"start": v(14.89, -24.44) * mm, "end": v(14.89, -18.1) * mm});
            skLineSegment(sketch, "E211.MirrorCS", {"start": v(91.09, -24.44) * mm, "end": v(91.09, -18.1) * mm});
            skLineSegment(sketch, "E212.MirrorCS", {"start": v(8.54, -62.54) * mm, "end": v(8.54, -56.2) * mm});
            skLineSegment(sketch, "E213.MirrorCS", {"start": v(-34, -49.84) * mm, "end": v(-27.65, -49.84) * mm});
            skLineSegment(sketch, "E214.MirrorCS", {"start": v(27.59, -81.6) * mm, "end": v(21.24, -81.6) * mm});
            skLineSegment(sketch, "E215.MirrorCS", {"start": v(8.54, -24.44) * mm, "end": v(8.54, -18.1) * mm});
            skLineSegment(sketch, "E216.MirrorCS", {"start": v(78.39, -37.14) * mm, "end": v(72.04, -37.14) * mm});
            skLineSegment(sketch, "E217.MirrorCS", {"start": v(-21.3, -68.9) * mm, "end": v(-14.95, -68.9) * mm});
            skLineSegment(sketch, "E218.MirrorCS", {"start": v(14.89, -30.8) * mm, "end": v(8.54, -30.8) * mm});
            skLineSegment(sketch, "E219.MirrorCS", {"start": v(-34, -24.44) * mm, "end": v(-27.65, -24.44) * mm});
            skLineSegment(sketch, "E220.MirrorCS", {"start": v(78.39, -37.14) * mm, "end": v(78.39, -30.8) * mm});
            skLineSegment(sketch, "E221.MirrorCS", {"start": v(65.69, -24.44) * mm, "end": v(65.69, -18.1) * mm});
            skLineSegment(sketch, "E222.MirrorCS", {"start": v(91.09, -18.1) * mm, "end": v(84.74, -18.1) * mm});
            skLineSegment(sketch, "E223.MirrorCS", {"start": v(84.74, -24.44) * mm, "end": v(84.74, -18.1) * mm});
            skLineSegment(sketch, "E224.MirrorCS", {"start": v(40.29, -24.44) * mm, "end": v(40.29, -18.1) * mm});
            skLineSegment(sketch, "E225.MirrorCS", {"start": v(-2.25, -49.84) * mm, "end": v(-2.25, -43.5) * mm});
            skLineSegment(sketch, "E226.MirrorCS", {"start": v(-21.3, -37.14) * mm, "end": v(-21.3, -30.8) * mm});
            skLineSegment(sketch, "E227.MirrorCS", {"start": v(-34, -30.8) * mm, "end": v(-27.65, -30.8) * mm});
            skLineSegment(sketch, "E228.MirrorCS", {"start": v(-34, -11.74) * mm, "end": v(-27.65, -11.74) * mm});
            skLineSegment(sketch, "E229.MirrorCS", {"start": v(-40.35, -62.54) * mm, "end": v(-40.35, -56.2) * mm});
            skLineSegment(sketch, "E230.MirrorCS", {"start": v(78.39, -11.74) * mm, "end": v(72.04, -11.74) * mm});
            skLineSegment(sketch, "E231.MirrorCS", {"start": v(-14.95, -24.44) * mm, "end": v(-14.95, -18.1) * mm});
            skLineSegment(sketch, "E232.MirrorCS", {"start": v(-84.8, -24.44) * mm, "end": v(-84.8, -18.1) * mm});
            skLineSegment(sketch, "E233.MirrorCS", {"start": v(-72.1, -24.44) * mm, "end": v(-72.1, -18.1) * mm});
            skLineSegment(sketch, "E234.MirrorCS", {"start": v(46.64, -24.44) * mm, "end": v(46.64, -18.1) * mm});
            skLineSegment(sketch, "E235.MirrorCS", {"start": v(14.89, -62.54) * mm, "end": v(8.54, -62.54) * mm});
            skLineSegment(sketch, "E236.MirrorCS", {"start": v(59.34, -24.44) * mm, "end": v(59.34, -18.1) * mm});
            skLineSegment(sketch, "E237.MirrorCS", {"start": v(14.89, -56.2) * mm, "end": v(8.54, -56.2) * mm});
            skLineSegment(sketch, "E238.MirrorCS", {"start": v(-8.6, -81.6) * mm, "end": v(-2.25, -81.6) * mm});
            skLineSegment(sketch, "E239.MirrorCS", {"start": v(46.64, -49.84) * mm, "end": v(46.64, -43.5) * mm});
            skLineSegment(sketch, "E240.MirrorCS", {"start": v(-59.4, -37.14) * mm, "end": v(-59.4, -30.8) * mm});
            skLineSegment(sketch, "E241.MirrorCS", {"start": v(27.59, -18.1) * mm, "end": v(21.24, -18.1) * mm});
            skLineSegment(sketch, "E242.MirrorCS", {"start": v(-8.6, -5.4) * mm, "end": v(-2.25, -5.4) * mm});
            skLineSegment(sketch, "E243.MirrorCS", {"start": v(-46.7, -62.54) * mm, "end": v(-46.7, -56.2) * mm});
            skLineSegment(sketch, "E244.MirrorCS", {"start": v(-72.1, -37.14) * mm, "end": v(-65.75, -37.14) * mm});
            skLineSegment(sketch, "E245.MirrorCS", {"start": v(-8.6, -30.8) * mm, "end": v(-2.25, -30.8) * mm});
            skLineSegment(sketch, "E246.MirrorCS", {"start": v(-21.3, -49.84) * mm, "end": v(-14.95, -49.84) * mm});
            skLineSegment(sketch, "E247.MirrorCS", {"start": v(-72.1, -5.4) * mm, "end": v(-65.75, -5.4) * mm});
            skLineSegment(sketch, "E248.MirrorCS", {"start": v(72.04, -24.44) * mm, "end": v(72.04, -18.1) * mm});
            skLineSegment(sketch, "E249.MirrorCS", {"start": v(52.99, -37.14) * mm, "end": v(52.99, -30.8) * mm});
            skLineSegment(sketch, "E250.MirrorCS", {"start": v(33.94, -37.14) * mm, "end": v(33.94, -30.8) * mm});
            skLineSegment(sketch, "E251.MirrorCS", {"start": v(40.29, -49.84) * mm, "end": v(33.94, -49.84) * mm});
            skLineSegment(sketch, "E252.MirrorCS", {"start": v(8.54, -49.84) * mm, "end": v(8.54, -43.5) * mm});
            skLineSegment(sketch, "E253.MirrorCS", {"start": v(27.59, -49.84) * mm, "end": v(21.24, -49.84) * mm});
            skLineSegment(sketch, "E254.MirrorCS", {"start": v(40.29, -5.4) * mm, "end": v(33.94, -5.4) * mm});
            skLineSegment(sketch, "E255.MirrorCS", {"start": v(-34, -24.44) * mm, "end": v(-34, -18.1) * mm});
            skLineSegment(sketch, "E256.MirrorCS", {"start": v(78.39, -43.5) * mm, "end": v(72.04, -43.5) * mm});
            skLineSegment(sketch, "E257.MirrorCS", {"start": v(91.09, -24.44) * mm, "end": v(84.74, -24.44) * mm});
            skLineSegment(sketch, "E258.MirrorCS", {"start": v(-21.3, -62.54) * mm, "end": v(-14.95, -62.54) * mm});
            skLineSegment(sketch, "E259.MirrorCS", {"start": v(-40.35, -37.14) * mm, "end": v(-40.35, -30.8) * mm});
            skLineSegment(sketch, "E260.MirrorCS", {"start": v(-53.05, -62.54) * mm, "end": v(-53.05, -56.2) * mm});
            skLineSegment(sketch, "E261.MirrorCS", {"start": v(-27.65, -24.44) * mm, "end": v(-27.65, -18.1) * mm});
            skLineSegment(sketch, "E262.MirrorCS", {"start": v(-84.8, -5.4) * mm, "end": v(-78.45, -5.4) * mm});
            skLineSegment(sketch, "E263.MirrorCS", {"start": v(40.29, -56.2) * mm, "end": v(33.94, -56.2) * mm});
            skLineSegment(sketch, "E264.MirrorCS", {"start": v(-14.95, -62.54) * mm, "end": v(-14.95, -56.2) * mm});
            skLineSegment(sketch, "E265.MirrorCS", {"start": v(-21.3, -87.94) * mm, "end": v(-14.95, -87.94) * mm});
            skLineSegment(sketch, "E266.MirrorCS", {"start": v(-21.3, -43.5) * mm, "end": v(-14.95, -43.5) * mm});
            skLineSegment(sketch, "E267.MirrorCS", {"start": v(52.99, -24.44) * mm, "end": v(52.99, -18.1) * mm});
            skLineSegment(sketch, "E268.MirrorCS", {"start": v(-34, -5.4) * mm, "end": v(-27.65, -5.4) * mm});
            skLineSegment(sketch, "E269.MirrorCS", {"start": v(14.89, -75.24) * mm, "end": v(8.54, -75.24) * mm});
            skLineSegment(sketch, "E270.MirrorCS", {"start": v(14.89, -49.84) * mm, "end": v(8.54, -49.84) * mm});
            skLineSegment(sketch, "E271.MirrorCS", {"start": v(27.59, -56.2) * mm, "end": v(21.24, -56.2) * mm});
            skLineSegment(sketch, "E272.MirrorCS", {"start": v(-65.75, -49.84) * mm, "end": v(-65.75, -43.5) * mm});
            skLineSegment(sketch, "E273.MirrorCS", {"start": v(-21.3, -24.44) * mm, "end": v(-14.95, -24.44) * mm});
            skLineSegment(sketch, "E274.MirrorCS", {"start": v(-21.3, -75.24) * mm, "end": v(-14.95, -75.24) * mm});
            skLineSegment(sketch, "E275.MirrorCS", {"start": v(-34, -62.54) * mm, "end": v(-27.65, -62.54) * mm});
            skLineSegment(sketch, "E276.MirrorCS", {"start": v(91.09, -37.14) * mm, "end": v(91.09, -30.8) * mm});
            skLineSegment(sketch, "E277.MirrorCS", {"start": v(27.59, -62.54) * mm, "end": v(27.59, -56.2) * mm});
            skLineSegment(sketch, "E278.MirrorCS", {"start": v(40.29, -43.5) * mm, "end": v(33.94, -43.5) * mm});
            skLineSegment(sketch, "E279.MirrorCS", {"start": v(78.39, -24.44) * mm, "end": v(72.04, -24.44) * mm});
            skLineSegment(sketch, "E280.MirrorCS", {"start": v(27.59, -37.14) * mm, "end": v(21.24, -37.14) * mm});
            skLineSegment(sketch, "E281.MirrorCS", {"start": v(8.54, -37.14) * mm, "end": v(8.54, -30.8) * mm});
            skLineSegment(sketch, "E282.MirrorCS", {"start": v(14.89, -81.6) * mm, "end": v(8.54, -81.6) * mm});
            skLineSegment(sketch, "E283.MirrorCS", {"start": v(91.09, -30.8) * mm, "end": v(84.74, -30.8) * mm});
            skLineSegment(sketch, "E284.MirrorCS", {"start": v(78.39, -24.44) * mm, "end": v(78.39, -18.1) * mm});
            skLineSegment(sketch, "E285.MirrorCS", {"start": v(14.89, -37.14) * mm, "end": v(14.89, -30.8) * mm});
            skLineSegment(sketch, "E286.MirrorCS", {"start": v(-21.3, -37.14) * mm, "end": v(-14.95, -37.14) * mm});
            skLineSegment(sketch, "E287.MirrorCS", {"start": v(-8.6, -75.24) * mm, "end": v(-2.25, -75.24) * mm});
            skLineSegment(sketch, "E288.MirrorCS", {"start": v(-8.6, -24.44) * mm, "end": v(-8.6, -18.1) * mm});
            skLineSegment(sketch, "E289.MirrorCS", {"start": v(65.69, -49.84) * mm, "end": v(65.69, -43.5) * mm});
            skLineSegment(sketch, "E290.MirrorCS", {"start": v(-72.1, -24.44) * mm, "end": v(-65.75, -24.44) * mm});
            skLineSegment(sketch, "E291.MirrorCS", {"start": v(27.59, -30.8) * mm, "end": v(21.24, -30.8) * mm});
            skLineSegment(sketch, "E292.MirrorCS", {"start": v(40.29, -81.6) * mm, "end": v(33.94, -81.6) * mm});
            skLineSegment(sketch, "E293.MirrorCS", {"start": v(52.99, -49.84) * mm, "end": v(52.99, -43.5) * mm});
            skLineSegment(sketch, "E294.MirrorCS", {"start": v(-8.6, -37.14) * mm, "end": v(-2.25, -37.14) * mm});
            skLineSegment(sketch, "E295.MirrorCS", {"start": v(-34, -37.14) * mm, "end": v(-27.65, -37.14) * mm});
            skLineSegment(sketch, "E296.MirrorCS", {"start": v(-8.6, -87.94) * mm, "end": v(-2.25, -87.94) * mm});
            skLineSegment(sketch, "E297.MirrorCS", {"start": v(84.74, -37.14) * mm, "end": v(84.74, -30.8) * mm});
            skLineSegment(sketch, "E298.MirrorCS", {"start": v(14.89, -18.1) * mm, "end": v(8.54, -18.1) * mm});
            skLineSegment(sketch, "E299.MirrorCS", {"start": v(91.09, -11.74) * mm, "end": v(84.74, -11.74) * mm});
            skLineSegment(sketch, "E300.MirrorCS", {"start": v(14.89, -87.94) * mm, "end": v(8.54, -87.94) * mm});
            skLineSegment(sketch, "E301.MirrorCS", {"start": v(-21.3, -5.4) * mm, "end": v(-14.95, -5.4) * mm});
            skLineSegment(sketch, "E302.MirrorCS", {"start": v(-2.25, -24.44) * mm, "end": v(-2.25, -18.1) * mm});
            skLineSegment(sketch, "E303.MirrorCS", {"start": v(46.64, -62.54) * mm, "end": v(46.64, -56.2) * mm});
            skLineSegment(sketch, "E304.MirrorCS", {"start": v(72.04, -37.14) * mm, "end": v(72.04, -30.8) * mm});
            skLineSegment(sketch, "E305.MirrorCS", {"start": v(78.39, -18.1) * mm, "end": v(72.04, -18.1) * mm});
            skLineSegment(sketch, "E306.MirrorCS", {"start": v(14.89, -24.44) * mm, "end": v(8.54, -24.44) * mm});
            skLineSegment(sketch, "E307.MirrorCS", {"start": v(-8.6, -24.44) * mm, "end": v(-2.25, -24.44) * mm});
            skLineSegment(sketch, "E308.MirrorCS", {"start": v(-8.6, -43.5) * mm, "end": v(-2.25, -43.5) * mm});
            skLineSegment(sketch, "E309.MirrorCS", {"start": v(-59.4, -49.84) * mm, "end": v(-59.4, -43.5) * mm});
            skLineSegment(sketch, "E310.MirrorCS", {"start": v(33.94, -62.54) * mm, "end": v(33.94, -56.2) * mm});
            skLineSegment(sketch, "E311.MirrorCS", {"start": v(-72.1, -37.14) * mm, "end": v(-72.1, -30.8) * mm});
            skLineSegment(sketch, "E312.MirrorCS", {"start": v(-21.3, -49.84) * mm, "end": v(-21.3, -43.5) * mm});
            skLineSegment(sketch, "E313.MirrorCS", {"start": v(-27.65, -49.84) * mm, "end": v(-27.65, -43.5) * mm});
            skLineSegment(sketch, "E314.MirrorCS", {"start": v(59.34, -62.54) * mm, "end": v(59.34, -56.2) * mm});
            skLineSegment(sketch, "E315.MirrorCS", {"start": v(-53.05, -24.44) * mm, "end": v(-53.05, -18.1) * mm});
            skLineSegment(sketch, "E316.MirrorCS", {"start": v(40.29, -18.1) * mm, "end": v(33.94, -18.1) * mm});
            skLineSegment(sketch, "E317.MirrorCS", {"start": v(21.24, -24.44) * mm, "end": v(21.24, -18.1) * mm});
            skLineSegment(sketch, "E318.MirrorCS", {"start": v(65.69, -37.14) * mm, "end": v(65.69, -30.8) * mm});
            skLineSegment(sketch, "E319.MirrorCS", {"start": v(-46.7, -49.84) * mm, "end": v(-46.7, -43.5) * mm});
            skLineSegment(sketch, "E320.MirrorCS", {"start": v(-34, -62.54) * mm, "end": v(-34, -56.2) * mm});
            skLineSegment(sketch, "E321.MirrorCS", {"start": v(-46.7, -24.44) * mm, "end": v(-46.7, -18.1) * mm});
            skLineSegment(sketch, "E322.MirrorCS", {"start": v(-14.95, -37.14) * mm, "end": v(-14.95, -30.8) * mm});
            skLineSegment(sketch, "E323.MirrorCS", {"start": v(-78.45, -24.44) * mm, "end": v(-78.45, -18.1) * mm});
            skLineSegment(sketch, "E324.MirrorCS", {"start": v(-59.4, -24.44) * mm, "end": v(-59.4, -18.1) * mm});
            skLineSegment(sketch, "E325.MirrorCS", {"start": v(40.29, -49.84) * mm, "end": v(40.29, -43.5) * mm});
            skLineSegment(sketch, "E326.MirrorCS", {"start": v(33.94, -49.84) * mm, "end": v(33.94, -43.5) * mm});
            skLineSegment(sketch, "E327.MirrorCS", {"start": v(91.09, -5.4) * mm, "end": v(84.74, -5.4) * mm});
            skLineSegment(sketch, "E328.MirrorCS", {"start": v(-2.25, -62.54) * mm, "end": v(-2.25, -56.2) * mm});
            skLineSegment(sketch, "E329.MirrorCS", {"start": v(-8.6, -62.54) * mm, "end": v(-8.6, -56.2) * mm});
            skLineSegment(sketch, "E330.MirrorCS", {"start": v(-21.3, -24.44) * mm, "end": v(-21.3, -18.1) * mm});
            skLineSegment(sketch, "E331.MirrorCS", {"start": v(40.29, -62.54) * mm, "end": v(33.94, -62.54) * mm});
            skLineSegment(sketch, "E332.MirrorCS", {"start": v(27.59, -87.94) * mm, "end": v(21.24, -87.94) * mm});
            skLineSegment(sketch, "E333.MirrorCS", {"start": v(14.89, -49.84) * mm, "end": v(14.89, -43.5) * mm});
            skLineSegment(sketch, "E334.MirrorCS", {"start": v(33.94, -24.44) * mm, "end": v(33.94, -18.1) * mm});
            skLineSegment(sketch, "E335.MirrorCS", {"start": v(-8.6, -37.14) * mm, "end": v(-8.6, -30.8) * mm});
            skLineSegment(sketch, "E336.MirrorCS", {"start": v(-8.6, -18.1) * mm, "end": v(-2.25, -18.1) * mm});
            skLineSegment(sketch, "E337.MirrorCS", {"start": v(-72.1, -43.5) * mm, "end": v(-65.75, -43.5) * mm});
            skLineSegment(sketch, "E338.MirrorCS", {"start": v(-78.45, -37.14) * mm, "end": v(-78.45, -30.8) * mm});
            skLineSegment(sketch, "E339.MirrorCS", {"start": v(-84.8, -24.44) * mm, "end": v(-78.45, -24.44) * mm});
            skLineSegment(sketch, "E340.MirrorCS", {"start": v(-8.6, -49.84) * mm, "end": v(-8.6, -43.5) * mm});
            skLineSegment(sketch, "E341.MirrorCS", {"start": v(-27.65, -37.14) * mm, "end": v(-27.65, -30.8) * mm});
            skLineSegment(sketch, "E342.MirrorCS", {"start": v(-84.8, -18.1) * mm, "end": v(-78.45, -18.1) * mm});
            skLineSegment(sketch, "E343.MirrorCS", {"start": v(-21.3, -62.54) * mm, "end": v(-21.3, -56.2) * mm});
            skLineSegment(sketch, "E344.MirrorCS", {"start": v(40.29, -62.54) * mm, "end": v(40.29, -56.2) * mm});
            skLineSegment(sketch, "E345.MirrorCS", {"start": v(-72.1, -49.84) * mm, "end": v(-72.1, -43.5) * mm});
            skLineSegment(sketch, "E346.MirrorCS", {"start": v(-34, -56.2) * mm, "end": v(-27.65, -56.2) * mm});
            skLineSegment(sketch, "E347.MirrorCS", {"start": v(-53.05, -37.14) * mm, "end": v(-53.05, -30.8) * mm});
            skLineSegment(sketch, "E348.MirrorCS", {"start": v(40.29, -30.8) * mm, "end": v(33.94, -30.8) * mm});
            skLineSegment(sketch, "E349.MirrorCS", {"start": v(40.29, -68.9) * mm, "end": v(33.94, -68.9) * mm});
            skLineSegment(sketch, "E350.MirrorCS", {"start": v(-34, -37.14) * mm, "end": v(-34, -30.8) * mm});
            skLineSegment(sketch, "E351.MirrorCS", {"start": v(52.99, -62.54) * mm, "end": v(52.99, -56.2) * mm});
            skLineSegment(sketch, "E352.MirrorCS", {"start": v(-34, -68.9) * mm, "end": v(-27.65, -68.9) * mm});
            skLineSegment(sketch, "E353.MirrorCS", {"start": v(-34, -18.1) * mm, "end": v(-27.65, -18.1) * mm});
            skLineSegment(sketch, "E354.MirrorCS", {"start": v(21.24, -49.84) * mm, "end": v(21.24, -43.5) * mm});
            skLineSegment(sketch, "E355.MirrorCS", {"start": v(-21.3, -56.2) * mm, "end": v(-14.95, -56.2) * mm});
            skLineSegment(sketch, "E356.MirrorCS", {"start": v(-34, -43.5) * mm, "end": v(-27.65, -43.5) * mm});
            skLineSegment(sketch, "E357.MirrorCS", {"start": v(27.59, -24.44) * mm, "end": v(27.59, -18.1) * mm});
            skLineSegment(sketch, "E358.MirrorCS", {"start": v(-46.7, -37.14) * mm, "end": v(-46.7, -30.8) * mm});
            skLineSegment(sketch, "E359.MirrorCS", {"start": v(-59.4, -62.54) * mm, "end": v(-59.4, -56.2) * mm});
            skLineSegment(sketch, "E360.MirrorCS", {"start": v(27.59, -75.24) * mm, "end": v(21.24, -75.24) * mm});
            skLineSegment(sketch, "E361.MirrorCS", {"start": v(40.29, -37.14) * mm, "end": v(40.29, -30.8) * mm});
            skLineSegment(sketch, "E362.MirrorCS", {"start": v(21.24, -62.54) * mm, "end": v(21.24, -56.2) * mm});
            skLineSegment(sketch, "E363.MirrorCS", {"start": v(-84.8, -30.8) * mm, "end": v(-78.45, -30.8) * mm});
            skLineSegment(sketch, "E364.MirrorCS", {"start": v(-84.8, -37.14) * mm, "end": v(-84.8, -30.8) * mm});
            skLineSegment(sketch, "E365.MirrorCS", {"start": v(27.59, -49.84) * mm, "end": v(27.59, -43.5) * mm});
            skLineSegment(sketch, "E366.MirrorCS", {"start": v(-21.3, -30.8) * mm, "end": v(-14.95, -30.8) * mm});
            skLineSegment(sketch, "E367.MirrorCS", {"start": v(-72.1, -18.1) * mm, "end": v(-65.75, -18.1) * mm});
            skLineSegment(sketch, "E368.MirrorCS", {"start": v(-21.3, -81.6) * mm, "end": v(-14.95, -81.6) * mm});
            skLineSegment(sketch, "E369.MirrorCS", {"start": v(14.89, -37.14) * mm, "end": v(8.54, -37.14) * mm});
            skLineSegment(sketch, "E370.MirrorCS", {"start": v(-8.6, -68.9) * mm, "end": v(-2.25, -68.9) * mm});
            skLineSegment(sketch, "E371.MirrorCS", {"start": v(-59.4, -30.8) * mm, "end": v(-53.05, -30.8) * mm});
            skLineSegment(sketch, "E372.MirrorCS", {"start": v(-59.4, -43.5) * mm, "end": v(-53.05, -43.5) * mm});
            skLineSegment(sketch, "E373.MirrorCS", {"start": v(-46.7, -68.9) * mm, "end": v(-40.35, -68.9) * mm});
            skLineSegment(sketch, "E374.MirrorCS", {"start": v(65.69, -24.44) * mm, "end": v(59.34, -24.44) * mm});
            skLineSegment(sketch, "E375.MirrorCS", {"start": v(65.69, -11.74) * mm, "end": v(59.34, -11.74) * mm});
            skLineSegment(sketch, "E376.MirrorCS", {"start": v(52.99, -68.9) * mm, "end": v(46.64, -68.9) * mm});
            skLineSegment(sketch, "E377.MirrorCS", {"start": v(65.69, -18.1) * mm, "end": v(59.34, -18.1) * mm});
            skLineSegment(sketch, "E378.MirrorCS", {"start": v(14.89, -11.74) * mm, "end": v(14.89, -5.4) * mm});
            skLineSegment(sketch, "E379.MirrorCS", {"start": v(-40.35, -75.24) * mm, "end": v(-40.35, -68.9) * mm});
            skLineSegment(sketch, "E380.MirrorCS", {"start": v(21.24, -11.74) * mm, "end": v(21.24, -5.4) * mm});
            skLineSegment(sketch, "E381.MirrorCS", {"start": v(-27.65, -11.74) * mm, "end": v(-27.65, -5.4) * mm});
            skLineSegment(sketch, "E382.MirrorCS", {"start": v(52.99, -30.8) * mm, "end": v(46.64, -30.8) * mm});
            skLineSegment(sketch, "E383.MirrorCS", {"start": v(-59.4, -49.84) * mm, "end": v(-53.05, -49.84) * mm});
            skLineSegment(sketch, "E384.MirrorCS", {"start": v(-46.7, -56.2) * mm, "end": v(-40.35, -56.2) * mm});
            skLineSegment(sketch, "E385.MirrorCS", {"start": v(-46.7, -5.4) * mm, "end": v(-40.35, -5.4) * mm});
            skLineSegment(sketch, "E386.MirrorCS", {"start": v(65.69, -37.14) * mm, "end": v(59.34, -37.14) * mm});
            skLineSegment(sketch, "E387.MirrorCS", {"start": v(-46.7, -37.14) * mm, "end": v(-40.35, -37.14) * mm});
            skLineSegment(sketch, "E388.MirrorCS", {"start": v(-46.7, -75.24) * mm, "end": v(-40.35, -75.24) * mm});
            skLineSegment(sketch, "E389.MirrorCS", {"start": v(-21.3, -87.94) * mm, "end": v(-21.3, -81.6) * mm});
            skLineSegment(sketch, "E390.MirrorCS", {"start": v(-2.25, -87.94) * mm, "end": v(-2.25, -81.6) * mm});
            skLineSegment(sketch, "E391.MirrorCS", {"start": v(-14.95, -75.24) * mm, "end": v(-14.95, -68.9) * mm});
            skLineSegment(sketch, "E392.MirrorCS", {"start": v(65.69, -43.5) * mm, "end": v(59.34, -43.5) * mm});
            skLineSegment(sketch, "E393.MirrorCS", {"start": v(40.29, -87.94) * mm, "end": v(40.29, -81.6) * mm});
            skLineSegment(sketch, "E394.MirrorCS", {"start": v(27.59, -75.24) * mm, "end": v(27.59, -68.9) * mm});
            skLineSegment(sketch, "E395.MirrorCS", {"start": v(52.99, -49.84) * mm, "end": v(46.64, -49.84) * mm});
            skLineSegment(sketch, "E396.MirrorCS", {"start": v(91.09, -11.74) * mm, "end": v(91.09, -5.4) * mm});
            skLineSegment(sketch, "E397.MirrorCS", {"start": v(-46.7, -49.84) * mm, "end": v(-40.35, -49.84) * mm});
            skLineSegment(sketch, "E398.MirrorCS", {"start": v(46.64, -75.24) * mm, "end": v(46.64, -68.9) * mm});
            skLineSegment(sketch, "E399.MirrorCS", {"start": v(33.94, -11.74) * mm, "end": v(33.94, -5.4) * mm});
            skLineSegment(sketch, "E400.MirrorCS", {"start": v(-14.95, -11.74) * mm, "end": v(-14.95, -5.4) * mm});
            skLineSegment(sketch, "E401.MirrorCS", {"start": v(-78.45, -11.74) * mm, "end": v(-78.45, -5.4) * mm});
            skLineSegment(sketch, "E402.MirrorCS", {"start": v(33.94, -75.24) * mm, "end": v(33.94, -68.9) * mm});
            skLineSegment(sketch, "E403.MirrorCS", {"start": v(21.24, -75.24) * mm, "end": v(21.24, -68.9) * mm});
            skLineSegment(sketch, "E404.MirrorCS", {"start": v(-8.6, -75.24) * mm, "end": v(-8.6, -68.9) * mm});
            skLineSegment(sketch, "E405.MirrorCS", {"start": v(-59.4, -24.44) * mm, "end": v(-53.05, -24.44) * mm});
            skLineSegment(sketch, "E406.MirrorCS", {"start": v(8.54, -75.24) * mm, "end": v(8.54, -68.9) * mm});
            skLineSegment(sketch, "E407.MirrorCS", {"start": v(-27.65, -87.94) * mm, "end": v(-27.65, -81.6) * mm});
            skLineSegment(sketch, "E408.MirrorCS", {"start": v(65.69, -5.4) * mm, "end": v(59.34, -5.4) * mm});
            skLineSegment(sketch, "E409.MirrorCS", {"start": v(52.99, -75.24) * mm, "end": v(46.64, -75.24) * mm});
            skLineSegment(sketch, "E410.MirrorCS", {"start": v(-53.05, -11.74) * mm, "end": v(-53.05, -5.4) * mm});
            skLineSegment(sketch, "E411.MirrorCS", {"start": v(-27.65, -75.24) * mm, "end": v(-27.65, -68.9) * mm});
            skLineSegment(sketch, "E412.MirrorCS", {"start": v(72.04, -11.74) * mm, "end": v(72.04, -5.4) * mm});
            skLineSegment(sketch, "E413.MirrorCS", {"start": v(-40.35, -11.74) * mm, "end": v(-40.35, -5.4) * mm});
            skLineSegment(sketch, "E414.MirrorCS", {"start": v(-46.7, -24.44) * mm, "end": v(-40.35, -24.44) * mm});
            skLineSegment(sketch, "E415.MirrorCS", {"start": v(-2.25, -11.74) * mm, "end": v(-2.25, -5.4) * mm});
            skLineSegment(sketch, "E416.MirrorCS", {"start": v(27.59, -87.94) * mm, "end": v(27.59, -81.6) * mm});
            skLineSegment(sketch, "E417.MirrorCS", {"start": v(52.99, -24.44) * mm, "end": v(46.64, -24.44) * mm});
            skLineSegment(sketch, "E418.MirrorCS", {"start": v(33.94, -87.94) * mm, "end": v(33.94, -81.6) * mm});
            skLineSegment(sketch, "E419.MirrorCS", {"start": v(59.34, -11.74) * mm, "end": v(59.34, -5.4) * mm});
            skLineSegment(sketch, "E420.MirrorCS", {"start": v(8.54, -87.94) * mm, "end": v(8.54, -81.6) * mm});
            skLineSegment(sketch, "E421.MirrorCS", {"start": v(52.99, -5.4) * mm, "end": v(46.64, -5.4) * mm});
            skLineSegment(sketch, "E422.MirrorCS", {"start": v(65.69, -30.8) * mm, "end": v(59.34, -30.8) * mm});
            skLineSegment(sketch, "E423.MirrorCS", {"start": v(84.74, -11.74) * mm, "end": v(84.74, -5.4) * mm});
            skLineSegment(sketch, "E424.MirrorCS", {"start": v(-46.7, -75.24) * mm, "end": v(-46.7, -68.9) * mm});
            skLineSegment(sketch, "E425.MirrorCS", {"start": v(-59.4, -11.74) * mm, "end": v(-53.05, -11.74) * mm});
            skLineSegment(sketch, "E426.MirrorCS", {"start": v(-59.4, -37.14) * mm, "end": v(-53.05, -37.14) * mm});
            skLineSegment(sketch, "E427.MirrorCS", {"start": v(-46.7, -62.54) * mm, "end": v(-40.35, -62.54) * mm});
            skLineSegment(sketch, "E428.MirrorCS", {"start": v(-46.7, -11.74) * mm, "end": v(-40.35, -11.74) * mm});
            skLineSegment(sketch, "E429.MirrorCS", {"start": v(52.99, -11.74) * mm, "end": v(52.99, -5.4) * mm});
            skLineSegment(sketch, "E430.MirrorCS", {"start": v(-59.4, -62.54) * mm, "end": v(-53.05, -62.54) * mm});
            skLineSegment(sketch, "E431.MirrorCS", {"start": v(-34, -11.74) * mm, "end": v(-34, -5.4) * mm});
            skLineSegment(sketch, "E432.MirrorCS", {"start": v(-84.8, -11.74) * mm, "end": v(-84.8, -5.4) * mm});
            skLineSegment(sketch, "E433.MirrorCS", {"start": v(52.99, -11.74) * mm, "end": v(46.64, -11.74) * mm});
            skLineSegment(sketch, "E434.MirrorCS", {"start": v(-34, -87.94) * mm, "end": v(-34, -81.6) * mm});
            skLineSegment(sketch, "E435.MirrorCS", {"start": v(-65.75, -11.74) * mm, "end": v(-65.75, -5.4) * mm});
            skLineSegment(sketch, "E436.MirrorCS", {"start": v(-14.95, -87.94) * mm, "end": v(-14.95, -81.6) * mm});
            skLineSegment(sketch, "E437.MirrorCS", {"start": v(78.39, -11.74) * mm, "end": v(78.39, -5.4) * mm});
            skLineSegment(sketch, "E438.MirrorCS", {"start": v(-2.25, -75.24) * mm, "end": v(-2.25, -68.9) * mm});
            skLineSegment(sketch, "E439.MirrorCS", {"start": v(65.69, -62.54) * mm, "end": v(59.34, -62.54) * mm});
            skLineSegment(sketch, "E440.MirrorCS", {"start": v(65.69, -49.84) * mm, "end": v(59.34, -49.84) * mm});
            skLineSegment(sketch, "E441.MirrorCS", {"start": v(65.69, -56.2) * mm, "end": v(59.34, -56.2) * mm});
            skLineSegment(sketch, "E442.MirrorCS", {"start": v(27.59, -11.74) * mm, "end": v(27.59, -5.4) * mm});
            skLineSegment(sketch, "E443.MirrorCS", {"start": v(40.29, -11.74) * mm, "end": v(40.29, -5.4) * mm});
            skLineSegment(sketch, "E444.MirrorCS", {"start": v(-46.7, -30.8) * mm, "end": v(-40.35, -30.8) * mm});
            skLineSegment(sketch, "E445.MirrorCS", {"start": v(-72.1, -11.74) * mm, "end": v(-72.1, -5.4) * mm});
            skLineSegment(sketch, "E446.MirrorCS", {"start": v(52.99, -75.24) * mm, "end": v(52.99, -68.9) * mm});
            skLineSegment(sketch, "E447.MirrorCS", {"start": v(-46.7, -43.5) * mm, "end": v(-40.35, -43.5) * mm});
            skLineSegment(sketch, "E448.MirrorCS", {"start": v(14.89, -75.24) * mm, "end": v(14.89, -68.9) * mm});
            skLineSegment(sketch, "E449.MirrorCS", {"start": v(-8.6, -87.94) * mm, "end": v(-8.6, -81.6) * mm});
            skLineSegment(sketch, "E450.MirrorCS", {"start": v(52.99, -56.2) * mm, "end": v(46.64, -56.2) * mm});
            skLineSegment(sketch, "E451.MirrorCS", {"start": v(52.99, -18.1) * mm, "end": v(46.64, -18.1) * mm});
            skLineSegment(sketch, "E452.MirrorCS", {"start": v(65.69, -11.74) * mm, "end": v(65.69, -5.4) * mm});
            skLineSegment(sketch, "E453.MirrorCS", {"start": v(52.99, -37.14) * mm, "end": v(46.64, -37.14) * mm});
            skLineSegment(sketch, "E454.MirrorCS", {"start": v(-21.3, -11.74) * mm, "end": v(-21.3, -5.4) * mm});
            skLineSegment(sketch, "E455.MirrorCS", {"start": v(52.99, -43.5) * mm, "end": v(46.64, -43.5) * mm});
            skLineSegment(sketch, "E456.MirrorCS", {"start": v(21.24, -87.94) * mm, "end": v(21.24, -81.6) * mm});
            skLineSegment(sketch, "E457.MirrorCS", {"start": v(-46.7, -18.1) * mm, "end": v(-40.35, -18.1) * mm});
            skLineSegment(sketch, "E458.MirrorCS", {"start": v(46.64, -11.74) * mm, "end": v(46.64, -5.4) * mm});
            skLineSegment(sketch, "E459.MirrorCS", {"start": v(-21.3, -75.24) * mm, "end": v(-21.3, -68.9) * mm});
            skLineSegment(sketch, "E460.MirrorCS", {"start": v(-34, -75.24) * mm, "end": v(-34, -68.9) * mm});
            skLineSegment(sketch, "E461.MirrorCS", {"start": v(40.29, -75.24) * mm, "end": v(40.29, -68.9) * mm});
            skLineSegment(sketch, "E462.MirrorCS", {"start": v(-59.4, -56.2) * mm, "end": v(-53.05, -56.2) * mm});
            skLineSegment(sketch, "E463.MirrorCS", {"start": v(8.54, -11.74) * mm, "end": v(8.54, -5.4) * mm});
            skLineSegment(sketch, "E464.MirrorCS", {"start": v(14.89, -87.94) * mm, "end": v(14.89, -81.6) * mm});
            skLineSegment(sketch, "E465.MirrorCS", {"start": v(-59.4, -5.4) * mm, "end": v(-53.05, -5.4) * mm});
            skLineSegment(sketch, "E466.MirrorCS", {"start": v(-59.4, -11.74) * mm, "end": v(-59.4, -5.4) * mm});
            skLineSegment(sketch, "E467.MirrorCS", {"start": v(-59.4, -18.1) * mm, "end": v(-53.05, -18.1) * mm});
            skLineSegment(sketch, "E468.MirrorCS", {"start": v(-46.7, -11.74) * mm, "end": v(-46.7, -5.4) * mm});
            skLineSegment(sketch, "E469.MirrorCS", {"start": v(52.99, -62.54) * mm, "end": v(46.64, -62.54) * mm});
            skLineSegment(sketch, "E470.MirrorCS", {"start": v(-8.6, -11.74) * mm, "end": v(-8.6, -5.4) * mm});
            skSolve(sketch);
        }
        {
            var Q0;
            Q0 = qSketchRegion(id + "F0", true);
            extrude(context, id + "F1", {"entities" : qUnion([Q0]), "depth" : 3.17 * mm});
        }
    });
